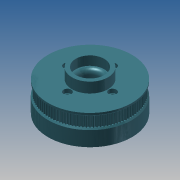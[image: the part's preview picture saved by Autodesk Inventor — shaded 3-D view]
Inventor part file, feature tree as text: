
AUTODESK INVENTOR PART (.ipt)
format: ipt  version: 2013 (Build 170138000, 138)  size: 1,295,360 bytes
history: native  units: mm
features: extrude x12, sketch x12, pattern_circular x2, chamfer x1, mirror x1, fillet x1
ambient origin geometry x8: Origin, YZ Plane, XZ Plane, XY Plane, X Axis, Y Axis, Z Axis, Center Point
bodies: Solid1 (feature_tree)
feature tree (29):
  extrude  "Extrusion1"  Depth=0.628319mm
  pattern_circular  "Circular Pattern1"  Count=100  [1 undecoded]
  extrude  "Extrusion3"  Depth=0.1mm
  chamfer  "Chamfer2"  Distance=2.5mm
  mirror  "Mirror1"
  extrude  "Extrusion7"  Depth=15.0mm
  extrude  "Extrusion8"  Depth=15.0mm
  extrude  "Extrusion9"  Depth=25.0mm
  extrude  "Extrusion10"  Depth=2.0mm TaperAngle=0.0deg
  extrude  "Extrusion11"  Depth=6.0mm
  pattern_circular  "Circular Pattern2"  [2 undecoded]
  extrude  "Extrusion12"  Depth=22.0mm
  fillet  "Fillet1"  Radius=7.0mm
  extrude  "Extrusion13"  Depth=1.0mm
  extrude  "Extrusion4"  Depth=28.0mm
  extrude  "Extrusion5"  Depth=8.0mm TaperAngle=0.0deg
  extrude  "Extrusion6"  Depth=15.0mm
  sketch  "Sketch1"  dims[d0=63.661977mm d9=0.628319mm]
  sketch  "Sketch3"  dims[d11=0.254mm]
  sketch  "Sketch4"  dims[d12=0.3mm]
  sketch  "Sketch5"  dims[d13=0.4mm]
  sketch  "Sketch6"  dims[d14=1.0mm]
  sketch  "Sketch7"  dims[d15=0.555mm]
  sketch  "Sketch8"  dims[d16=0.75mm]
  sketch  "Sketch9"  dims[d17=0.254mm]
  sketch  "Sketch10"  dims[d18=8.0mm d19=0.0mm d20=1000.0mm]
  sketch  "Sketch11"  dims[d21=360.0deg d23=0.1mm d32=2.5mm d33=0.0mm]
  sketch  "Sketch12"  dims[d34=1.0mm d35=2.0mm d36=45.0deg d37=15.0mm]
  sketch  "Sketch13"  dims[d39=3.5mm d40=15.0mm d41=25.0mm d42=2.0mm d43=0.0mm d44=6.0mm d46=3.0mm d47=0.0mm d49=22.0mm d51=7.0mm d52=0.0mm d53=1.0mm d54=28.0mm d56=8.0mm d57=0.0mm d58=15.0mm d60=10.0mm d61=0.0mm d62=22.0mm d64=7.0mm d65=0.0mm d68=17.5mm d69=3.5mm d70=7.0mm d71=0.0mm d72=6.0mm d74=3.0mm d75=0.0mm d76=40.0mm d77=360.0deg d80=10.0mm d81=0.0mm d82=3.5mm d83=65.0mm d85=10.0mm d86=0.0mm]
note: 3 required parameter values undecoded (feature->parameter linkage not recoverable at this tier; creation-order binding heuristic only, values carry confidence <= 0.55)
